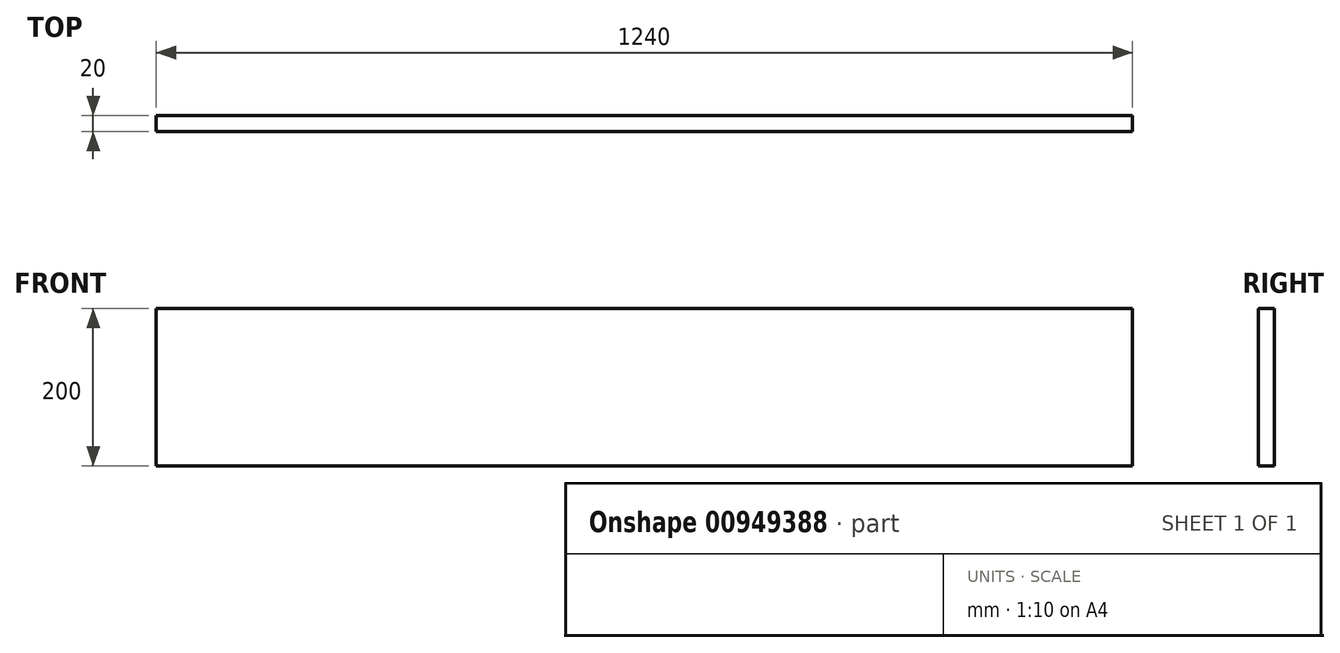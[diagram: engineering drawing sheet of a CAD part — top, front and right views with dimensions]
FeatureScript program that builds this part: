
annotation { "Feature Type Name" : "Feature", "Feature Type Description" : "" }
export const myFeature = defineFeature(function(context is Context, id is Id, definition is map)
    precondition{}
    {
        {
            var Q0;
            Q0=qCreatedBy(makeId("Front.planeOp"),FACE);
            var sketch = newSketch(context, id + "F0", { "sketchPlane" : qUnion([Q0])});
            skLineSegment(sketch, "E0.bottom", {"start": v(-616.9, -40.38) * mm, "end": v(623.1, -40.38) * mm});
            skLineSegment(sketch, "E0.top", {"start": v(-616.9, -240.38) * mm, "end": v(623.1, -240.38) * mm});
            skLineSegment(sketch, "E0.left", {"start": v(-616.9, -40.38) * mm, "end": v(-616.9, -240.38) * mm});
            skLineSegment(sketch, "E0.right", {"start": v(623.1, -40.38) * mm, "end": v(623.1, -240.38) * mm});
            skSolve(sketch);
        }
        {
            var Q0;
            Q0 = qSketchRegion(id + "F0", true);
            extrude(context, id + "F1", {"entities" : qUnion([Q0]), "depth" : 20 * mm, "offsetDistance" : 25 * mm});
        }
    });
